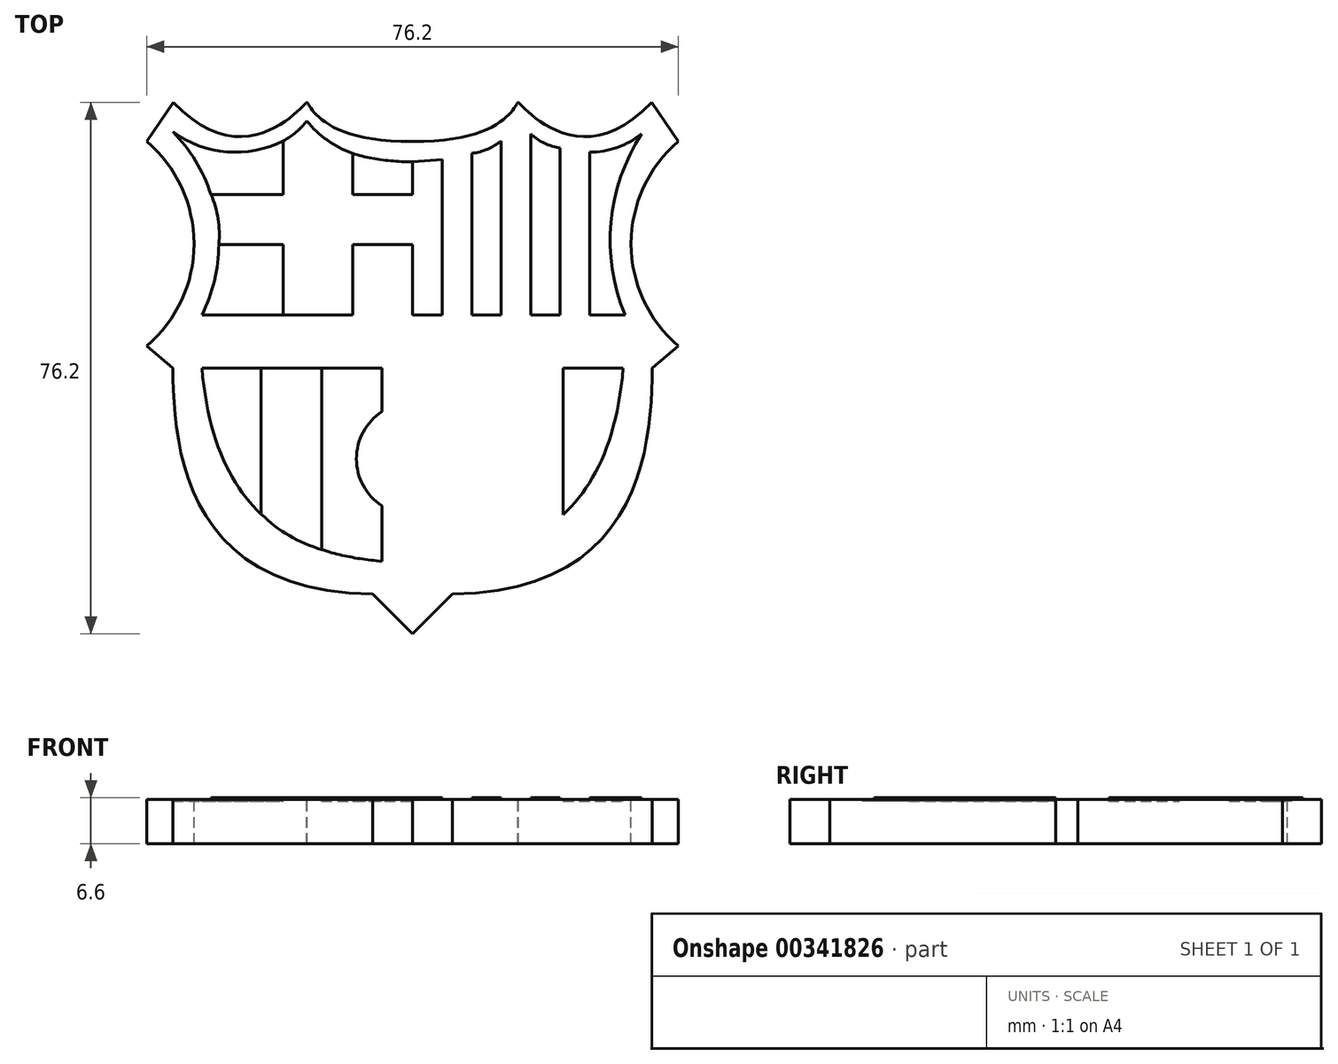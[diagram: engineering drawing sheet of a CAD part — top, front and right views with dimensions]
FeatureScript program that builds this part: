
annotation { "Feature Type Name" : "Feature", "Feature Type Description" : "" }
export const myFeature = defineFeature(function(context is Context, id is Id, definition is map)
    precondition{}
    {
        {
            var Q0;
            Q0=qCreatedBy(makeId("Top.planeOp"),FACE);
            var sketch = newSketch(context, id + "F0", { "sketchPlane" : qUnion([Q0])});
            skLineSegment(sketch, "E0.bottom", {"start": v(-19.05, -38.1) * mm, "end": v(19.05, -38.1) * mm});
            skLineSegment(sketch, "E0.top", {"start": v(-19.05, 38.1) * mm, "end": v(19.05, 38.1) * mm});
            skLineSegment(sketch, "E0.left", {"start": v(-19.05, -38.1) * mm, "end": v(-19.05, 38.1) * mm});
            skLineSegment(sketch, "E0.right", {"start": v(19.05, -38.1) * mm, "end": v(19.05, 38.1) * mm});
            skPoint(sketch, "E0.middle", {"position": v(0, 0) * mm});
            skSolve(sketch);
        }
        {
            var Q0;
            Q0=makeQuery(id+"F0.imprint","IMPRINT",FACE,{"disambiguationData":[TD([[makeQuery(id+"F0.imprint","IMPRINT",EDGE,{"derivedFrom":sQuery(id+"F0.wireOp",EDGE,"E0.bottom")}),1.0]])]});
            extrude(context, id + "F1", {"entities" : qUnion([Q0]), "depth" : 6.35 * mm});
        }
        {
            var Q0;
            Q0=makeQuery(id+"F1.opExtrude","CAP_FACE",FACE,{"disambiguationData":[OSD([sQuery(id+"F0.wireOp",EDGE,"E0.bottom"),sQuery(id+"F0.wireOp",EDGE,"E0.top"),sQuery(id+"F0.wireOp",EDGE,"E0.left"),sQuery(id+"F0.wireOp",EDGE,"E0.right")])],"isStart":false});
            var sketch = newSketch(context, id + "F2", { "sketchPlane" : qUnion([Q0])});
            skArc(sketch, "E1", {"start": v(19.05, 32.51) * mm, "mid": v(12.28, 17.83) * mm, "end": v(19.05, 3.15) * mm});
            skFitSpline(sketch, "E2", {"points": [v(-19.05, 32.51) * mm, v(-3.95, 38.1) * mm, v(-3.79, 38.03) * mm, v(15.22, 38.1) * mm], "startDerivative": vector(85.07, -1.32) * mm, "endDerivative": vector(60.07, 63.46) * mm});
            skLineSegment(sketch, "E3", {"start": v(15.22, 38.1) * mm, "end": v(19.05, 32.51) * mm});
            skLineSegment(sketch, "E4", {"start": v(19.05, 3.15) * mm, "end": v(15.33, 0) * mm});
            skFitSpline(sketch, "E5", {"points": [v(15.33, 0) * mm, v(-13.36, -32.4) * mm], "startDerivative": vector(-0.49, -34.46) * mm, "endDerivative": vector(-81.2, -0.97) * mm});
            skLineSegment(sketch, "E6", {"start": v(-13.36, -32.4) * mm, "end": v(-19.05, -38.1) * mm});
            skLineSegment(sketch, "E7", {"start": v(-19.05, 32.51) * mm, "end": v(-19.05, -38.1) * mm});
            skSolve(sketch);
        }
        {
            var Q0;
            {var subQ0=sQuery(id+"F2.wireOp",EDGE,"E2");var subQ1=makeQuery(id+"F1.opExtrude","CAP_EDGE",EDGE,{"disambiguationData":[OSD([sQuery(id+"F0.wireOp",EDGE,"E0.top")])],"isStart":false});var subQ2=makeQuery(id+"F2.imprint","INTERSECT",VERTEX,{"disambiguationData":[OD(0.0)],"derivedFrom":[subQ1,subQ0]});Q0=makeQuery(id+"F2.imprint","IMPRINT",FACE,{"disambiguationData":[TD([[makeQuery(id+"F2.imprint","IMPRINT",EDGE,{"disambiguationData":[TD([[subQ2,-1.0]])],"derivedFrom":subQ0}),-1.0]])]});}
            var Q1;
            {var subQ1=makeQuery(id+"F1.opExtrude","CAP_EDGE",EDGE,{"disambiguationData":[OSD([sQuery(id+"F0.wireOp",EDGE,"E0.left")])],"isStart":false});var subQ3=makeQuery(id+"F1.opExtrude","CAP_EDGE",EDGE,{"disambiguationData":[OSD([sQuery(id+"F0.wireOp",EDGE,"E0.top")])],"isStart":false});var subQ5=makeQuery(id+"F2.imprint","INTERSECT",VERTEX,{"derivedFrom":[subQ3,subQ1]});Q1=makeQuery(id+"F2.imprint","IMPRINT",FACE,{"disambiguationData":[TD([[makeQuery(id+"F2.imprint","IMPRINT",EDGE,{"disambiguationData":[TD([[subQ5,-1.0]])],"derivedFrom":subQ3}),-1.0]])]});}
            var Q2;
            {var subQ1=sQuery(id+"F2.wireOp",EDGE,"E4");Q2=makeQuery(id+"F2.imprint","IMPRINT",FACE,{"disambiguationData":[TD([[makeQuery(id+"F2.imprint","IMPRINT",EDGE,{"derivedFrom":subQ1}),1.0]])]});}
            var Q3;
            {var subQ0=sQuery(id+"F2.wireOp",EDGE,"E1");Q3=makeQuery(id+"F2.imprint","IMPRINT",FACE,{"disambiguationData":[TD([[makeQuery(id+"F2.imprint","IMPRINT",EDGE,{"derivedFrom":subQ0}),1.0]])]});}
            var Q4;
            {var subQ0=sQuery(id+"F2.wireOp",EDGE,"E3");Q4=makeQuery(id+"F2.imprint","IMPRINT",FACE,{"disambiguationData":[TD([[makeQuery(id+"F2.imprint","IMPRINT",EDGE,{"derivedFrom":subQ0}),1.0]])]});}
            var Q5;
            {var subQ0=sQuery(id+"F2.wireOp",EDGE,"E2");var subQ1=makeQuery(id+"F1.opExtrude","CAP_EDGE",EDGE,{"disambiguationData":[OSD([sQuery(id+"F0.wireOp",EDGE,"E0.top")])],"isStart":false});var subQ3=makeQuery(id+"F2.imprint","INTERSECT",VERTEX,{"disambiguationData":[OD(1.0)],"derivedFrom":[subQ1,subQ0]});Q5=makeQuery(id+"F2.imprint","IMPRINT",FACE,{"disambiguationData":[TD([[makeQuery(id+"F2.imprint","IMPRINT",EDGE,{"disambiguationData":[TD([[subQ3,-1.0]])],"derivedFrom":subQ0}),1.0]])]});}
            extrude(context, id + "F3", {"entities" : qUnion([Q0, Q1, Q2, Q3, Q4, Q5]), "operationType" : NewBodyOperationType.REMOVE, "oppositeDirection" : true, "depth" : 6.35 * mm});
        }
        {
            var Q0;
            Q0=makeQuery(id+"F1.opExtrude","SWEPT_BODY",BODY,{"disambiguationData":[OSD([sQuery(id+"F0.wireOp",EDGE,"E0.bottom"),sQuery(id+"F0.wireOp",EDGE,"E0.top"),sQuery(id+"F0.wireOp",EDGE,"E0.left"),sQuery(id+"F0.wireOp",EDGE,"E0.right")])]});
            var Q1;
            Q1=makeQuery(id+"F1.opExtrude","SWEPT_FACE",FACE,{"disambiguationData":[OSD([sQuery(id+"F0.wireOp",EDGE,"E0.left")])]});
            mirror(context, id + "F4", {"operationType" : NewBodyOperationType.ADD, "entities" : qUnion([Q0]), "mirrorPlane" : qUnion([Q1])});
        }
        {
            var Q0;
            {var subQ0=makeQuery(id+"F1.opExtrude","CAP_FACE",FACE,{"disambiguationData":[OSD([sQuery(id+"F0.wireOp",EDGE,"E0.bottom"),sQuery(id+"F0.wireOp",EDGE,"E0.top"),sQuery(id+"F0.wireOp",EDGE,"E0.left"),sQuery(id+"F0.wireOp",EDGE,"E0.right")])],"isStart":false});Q0=makeQuery(id+"F4.boolean.opBoolean","MERGE",FACE,{"derivedFrom":[subQ0,makeQuery(id+"F4.opPattern","COPY",FACE,{"derivedFrom":subQ0,"instanceName":"1"})]});}
            var sketch = newSketch(context, id + "F5", { "sketchPlane" : qUnion([Q0])});
            skArc(sketch, "E8", {"start": v(-53.4, 33.87) * mm, "mid": v(-43.7, 30.98) * mm, "end": v(-34.33, 34.8) * mm});
            skArc(sketch, "E9", {"start": v(15.17, 33.73) * mm, "mid": v(5.65, 30.98) * mm, "end": v(-3.56, 34.66) * mm});
            skFitSpline(sketch, "E10", {"points": [v(-34.33, 34.8) * mm, v(-3.56, 34.66) * mm], "startDerivative": vector(16.22, -20.16) * mm, "endDerivative": vector(21, 21.01) * mm});
            skArc(sketch, "E11", {"start": v(15.17, 33.73) * mm, "mid": v(9, 21.31) * mm, "end": v(11.14, 7.6) * mm});
            skArc(sketch, "E12", {"start": v(-53.4, 33.87) * mm, "mid": v(-47.11, 21.4) * mm, "end": v(-49.24, 7.6) * mm});
            skLineSegment(sketch, "E13", {"start": v(-49.24, 7.6) * mm, "end": v(11.14, 7.6) * mm});
            skLineSegment(sketch, "E14", {"start": v(-49.24, 0) * mm, "end": v(11.14, 0) * mm});
            skFitSpline(sketch, "E15", {"points": [v(-49.24, 0) * mm, v(-19.05, -27.87) * mm, v(11.14, 0) * mm], "startDerivative": vector(11.4, -138.75) * mm, "endDerivative": vector(11.4, 138.75) * mm});
            skLineSegment(sketch, "E16", {"start": v(-49.24, 0) * mm, "end": v(-40.74, 0) * mm});
            skLineSegment(sketch, "E17", {"start": v(-40.74, 0) * mm, "end": v(-40.74, -20.94) * mm});
            skLineSegment(sketch, "E18", {"start": v(-40.74, 0) * mm, "end": v(-32.09, 0) * mm});
            skLineSegment(sketch, "E19", {"start": v(-32.09, 0) * mm, "end": v(-32.09, -26.01) * mm});
            skLineSegment(sketch, "E20", {"start": v(-32.09, 0) * mm, "end": v(-23.43, 0) * mm});
            skLineSegment(sketch, "E21", {"start": v(-23.43, 0) * mm, "end": v(-14.78, 0) * mm});
            skLineSegment(sketch, "E22", {"start": v(-14.78, 0) * mm, "end": v(-6.12, 0) * mm});
            skLineSegment(sketch, "E23", {"start": v(-6.12, 0) * mm, "end": v(-6.12, -26.05) * mm});
            skLineSegment(sketch, "E24", {"start": v(-6.12, 0) * mm, "end": v(2.53, 0) * mm});
            skLineSegment(sketch, "E25", {"start": v(2.53, 0) * mm, "end": v(2.53, -21.04) * mm});
            skCircle(sketch, "E26", {"center": v(-19.05, -13) * mm, "radius": 8.05 * mm});
            skPoint(sketch, "E26.centerSnap0", {"position": v(-32.09, -13) * mm});
            skLineSegment(sketch, "E27", {"start": v(-23.43, 0) * mm, "end": v(-23.43, -6.26) * mm});
            skLineSegment(sketch, "E28", {"start": v(-23.43, -19.75) * mm, "end": v(-23.43, -27.7) * mm});
            skLineSegment(sketch, "E29", {"start": v(-14.78, 0) * mm, "end": v(-14.78, -6.19) * mm});
            skLineSegment(sketch, "E30", {"start": v(-14.78, -19.82) * mm, "end": v(-14.78, -27.7) * mm});
            skLineSegment(sketch, "E31", {"start": v(-19.05, 7.6) * mm, "end": v(-19.05, 29.58) * mm});
            skLineSegment(sketch, "E32", {"start": v(-19.05, 7.6) * mm, "end": v(-14.78, 7.6) * mm});
            skLineSegment(sketch, "E33", {"start": v(-14.78, 7.6) * mm, "end": v(-10.56, 7.6) * mm});
            skLineSegment(sketch, "E34", {"start": v(-10.56, 7.6) * mm, "end": v(-6.33, 7.6) * mm});
            skLineSegment(sketch, "E35", {"start": v(-6.33, 7.6) * mm, "end": v(-2.11, 7.6) * mm});
            skLineSegment(sketch, "E36", {"start": v(-2.11, 7.6) * mm, "end": v(2.11, 7.6) * mm});
            skLineSegment(sketch, "E37", {"start": v(2.11, 7.6) * mm, "end": v(6.33, 7.6) * mm});
            skLineSegment(sketch, "E38", {"start": v(6.33, 7.6) * mm, "end": v(6.33, 30.96) * mm});
            skLineSegment(sketch, "E39", {"start": v(2.11, 7.6) * mm, "end": v(2.11, 31.57) * mm});
            skLineSegment(sketch, "E40", {"start": v(-2.11, 7.6) * mm, "end": v(-2.11, 33.56) * mm});
            skLineSegment(sketch, "E41", {"start": v(-6.33, 7.6) * mm, "end": v(-6.33, 32.57) * mm});
            skLineSegment(sketch, "E42", {"start": v(-10.56, 6.12) * mm, "end": v(-10.56, 30.78) * mm});
            skLineSegment(sketch, "E43", {"start": v(-14.78, 7.6) * mm, "end": v(-14.78, 29.88) * mm});
            skLineSegment(sketch, "E44.bottom", {"start": v(-19.05, 7.6) * mm, "end": v(-27.66, 7.6) * mm});
            skLineSegment(sketch, "E44.top", {"start": v(-19.05, 17.73) * mm, "end": v(-27.66, 17.73) * mm});
            skLineSegment(sketch, "E44.left", {"start": v(-19.05, 7.6) * mm, "end": v(-19.05, 17.73) * mm});
            skLineSegment(sketch, "E44.right", {"start": v(-27.66, 7.6) * mm, "end": v(-27.66, 17.73) * mm});
            skLineSegment(sketch, "E45", {"start": v(-27.66, 30.77) * mm, "end": v(-27.66, 24.91) * mm});
            skLineSegment(sketch, "E46", {"start": v(-27.66, 24.91) * mm, "end": v(-19.05, 24.91) * mm});
            skLineSegment(sketch, "E47", {"start": v(-27.66, 7.6) * mm, "end": v(-37.58, 7.6) * mm});
            skLineSegment(sketch, "E48", {"start": v(-37.58, 7.6) * mm, "end": v(-37.58, 17.73) * mm});
            skLineSegment(sketch, "E49", {"start": v(-37.58, 17.73) * mm, "end": v(-46.83, 17.73) * mm});
            skLineSegment(sketch, "E50", {"start": v(-37.58, 24.91) * mm, "end": v(-37.58, 32.6) * mm});
            skLineSegment(sketch, "E51", {"start": v(-37.58, 24.91) * mm, "end": v(-47.95, 24.91) * mm});
            skSolve(sketch);
        }
        {
            var Q0;
            {var subQ3=sQuery(id+"F5.wireOp",EDGE,"E50");Q0=makeQuery(id+"F5.imprint","IMPRINT",FACE,{"disambiguationData":[TD([[makeQuery(id+"F5.imprint","IMPRINT",EDGE,{"derivedFrom":subQ3}),1.0]])]});}
            var Q1;
            {var subQ4=sQuery(id+"F5.wireOp",EDGE,"E48");Q1=makeQuery(id+"F5.imprint","IMPRINT",FACE,{"disambiguationData":[TD([[makeQuery(id+"F5.imprint","IMPRINT",EDGE,{"derivedFrom":subQ4}),1.0]])]});}
            var Q2;
            Q2=makeQuery(id+"F5.imprint","IMPRINT",FACE,{"disambiguationData":[TD([[makeQuery(id+"F5.imprint","IMPRINT",EDGE,{"derivedFrom":sQuery(id+"F5.wireOp",EDGE,"E44.bottom")}),-1.0]])]});
            var Q3;
            {var subQ3=sQuery(id+"F5.wireOp",EDGE,"E45");Q3=makeQuery(id+"F5.imprint","IMPRINT",FACE,{"disambiguationData":[TD([[makeQuery(id+"F5.imprint","IMPRINT",EDGE,{"derivedFrom":subQ3}),1.0]])]});}
            var Q4;
            {var subQ4=sQuery(id+"F5.wireOp",EDGE,"E33");Q4=makeQuery(id+"F5.imprint","IMPRINT",FACE,{"disambiguationData":[TD([[makeQuery(id+"F5.imprint","IMPRINT",EDGE,{"derivedFrom":subQ4}),1.0]])]});}
            var Q5;
            Q5=makeQuery(id+"F5.imprint","IMPRINT",FACE,{"disambiguationData":[TD([[makeQuery(id+"F5.imprint","IMPRINT",EDGE,{"derivedFrom":sQuery(id+"F5.wireOp",EDGE,"E35")}),1.0]])]});
            var Q6;
            Q6=makeQuery(id+"F5.imprint","IMPRINT",FACE,{"disambiguationData":[TD([[makeQuery(id+"F5.imprint","IMPRINT",EDGE,{"derivedFrom":sQuery(id+"F5.wireOp",EDGE,"E37")}),1.0]])]});
            var Q7;
            {var subQ0=sQuery(id+"F5.wireOp",EDGE,"E14");Q7=makeQuery(id+"F5.imprint","IMPRINT",FACE,{"disambiguationData":[TD([[makeQuery(id+"F5.imprint","IMPRINT",EDGE,{"derivedFrom":subQ0}),-1.0]])]});}
            var Q8;
            Q8=makeQuery(id+"F5.imprint","IMPRINT",FACE,{"disambiguationData":[TD([[makeQuery(id+"F5.imprint","IMPRINT",EDGE,{"derivedFrom":sQuery(id+"F5.wireOp",EDGE,"E22")}),-1.0]])]});
            var Q9;
            {var subQ3=sQuery(id+"F5.wireOp",EDGE,"E19");Q9=makeQuery(id+"F5.imprint","IMPRINT",FACE,{"disambiguationData":[TD([[makeQuery(id+"F5.imprint","IMPRINT",EDGE,{"derivedFrom":subQ3}),1.0]])]});}
            var Q10;
            {var subQ0=sQuery(id+"F5.wireOp",EDGE,"E16");Q10=makeQuery(id+"F5.imprint","IMPRINT",FACE,{"disambiguationData":[TD([[makeQuery(id+"F5.imprint","IMPRINT",EDGE,{"derivedFrom":subQ0}),-1.0]])]});}
            extrude(context, id + "F6", {"entities" : qUnion([Q0, Q1, Q2, Q3, Q4, Q5, Q6, Q7, Q8, Q9, Q10]), "operationType" : NewBodyOperationType.REMOVE, "oppositeDirection" : true, "depth" : 0.25 * mm});
        }
        {
            var Q0;
            {var subQ0=makeQuery(id+"F1.opExtrude","CAP_FACE",FACE,{"disambiguationData":[OSD([sQuery(id+"F0.wireOp",EDGE,"E0.bottom"),sQuery(id+"F0.wireOp",EDGE,"E0.top"),sQuery(id+"F0.wireOp",EDGE,"E0.left"),sQuery(id+"F0.wireOp",EDGE,"E0.right")])],"isStart":false});Q0=makeQuery(id+"F4.boolean.opBoolean","MERGE",FACE,{"derivedFrom":[subQ0,makeQuery(id+"F4.opPattern","COPY",FACE,{"derivedFrom":subQ0,"instanceName":"1"})]});}
            var sketch = newSketch(context, id + "F7", { "sketchPlane" : qUnion([Q0])});
            skLineSegment(sketch, "E52", {"start": v(-37.58, 7.6) * mm, "end": v(-27.66, 7.6) * mm});
            skLineSegment(sketch, "E53", {"start": v(-27.66, 7.6) * mm, "end": v(-27.66, 17.73) * mm});
            skLineSegment(sketch, "E54", {"start": v(-27.66, 17.73) * mm, "end": v(-19.05, 17.73) * mm});
            skLineSegment(sketch, "E55", {"start": v(-19.05, 17.73) * mm, "end": v(-19.05, 24.91) * mm});
            skLineSegment(sketch, "E56", {"start": v(-19.05, 24.91) * mm, "end": v(-27.66, 24.91) * mm});
            skLineSegment(sketch, "E57", {"start": v(-27.66, 24.91) * mm, "end": v(-27.66, 30.77) * mm});
            skArc(sketch, "E58", {"start": v(-46.83, 17.73) * mm, "mid": v(-46.93, 21.4) * mm, "end": v(-47.95, 24.91) * mm});
            skArc(sketch, "E59", {"start": v(-40.74, -20.94) * mm, "mid": v(-36.74, -24.02) * mm, "end": v(-32.09, -26.01) * mm});
            skArc(sketch, "E60", {"start": v(-23.43, -27.7) * mm, "mid": v(-19.1, -28.08) * mm, "end": v(-14.78, -27.7) * mm});
            skArc(sketch, "E61", {"start": v(-6.12, -26.05) * mm, "mid": v(-1.39, -24.25) * mm, "end": v(2.53, -21.04) * mm});
            skLineSegment(sketch, "E62", {"start": v(-47.95, 24.91) * mm, "end": v(-37.58, 24.91) * mm});
            skLineSegment(sketch, "E63", {"start": v(-37.58, 24.91) * mm, "end": v(-37.58, 32.6) * mm});
            skLineSegment(sketch, "E64", {"start": v(-46.83, 17.73) * mm, "end": v(-37.58, 17.73) * mm});
            skLineSegment(sketch, "E65", {"start": v(-37.58, 17.73) * mm, "end": v(-37.58, 7.6) * mm});
            skLineSegment(sketch, "E66", {"start": v(-40.74, 0) * mm, "end": v(-32.09, 0) * mm});
            skLineSegment(sketch, "E67", {"start": v(-32.09, 0) * mm, "end": v(-32.09, -26.01) * mm});
            skLineSegment(sketch, "E68", {"start": v(-40.74, 0) * mm, "end": v(-40.74, -20.94) * mm});
            skLineSegment(sketch, "E69", {"start": v(-23.43, 0) * mm, "end": v(-14.78, 0) * mm});
            skLineSegment(sketch, "E70", {"start": v(-6.12, 0) * mm, "end": v(2.53, 0) * mm});
            skLineSegment(sketch, "E71", {"start": v(-19.05, 7.6) * mm, "end": v(-14.78, 7.6) * mm});
            skLineSegment(sketch, "E72", {"start": v(-14.78, 7.6) * mm, "end": v(-14.78, 29.88) * mm});
            skLineSegment(sketch, "E73", {"start": v(-14.78, 29.88) * mm, "end": v(-19.05, 29.58) * mm});
            skLineSegment(sketch, "E74", {"start": v(-19.05, 29.58) * mm, "end": v(-19.05, 7.6) * mm});
            skLineSegment(sketch, "E75", {"start": v(-10.56, 7.6) * mm, "end": v(-6.33, 7.6) * mm});
            skLineSegment(sketch, "E76", {"start": v(-6.33, 7.6) * mm, "end": v(-6.33, 32.57) * mm});
            skArc(sketch, "E77", {"start": v(-10.56, 30.78) * mm, "mid": v(-8.32, 31.38) * mm, "end": v(-6.33, 32.57) * mm});
            skLineSegment(sketch, "E78", {"start": v(-10.56, 30.78) * mm, "end": v(-10.56, 7.6) * mm});
            skLineSegment(sketch, "E79", {"start": v(-2.11, 7.6) * mm, "end": v(2.11, 7.6) * mm});
            skLineSegment(sketch, "E80", {"start": v(2.11, 7.6) * mm, "end": v(2.11, 31.57) * mm});
            skLineSegment(sketch, "E81", {"start": v(-2.11, 7.6) * mm, "end": v(-2.11, 33.56) * mm});
            skArc(sketch, "E82", {"start": v(-2.11, 33.56) * mm, "mid": v(-0.15, 32.25) * mm, "end": v(2.11, 31.57) * mm});
            skArc(sketch, "E83", {"start": v(6.33, 30.96) * mm, "mid": v(10.29, 31.63) * mm, "end": v(13.79, 33.59) * mm});
            skLineSegment(sketch, "E84", {"start": v(6.33, 7.6) * mm, "end": v(11.4, 7.6) * mm});
            skArc(sketch, "E85", {"start": v(13.79, 33.59) * mm, "mid": v(9.4, 20.9) * mm, "end": v(11.4, 7.6) * mm});
            skLineSegment(sketch, "E86", {"start": v(6.33, 30.96) * mm, "end": v(6.33, 7.6) * mm});
            skPoint(sketch, "E87", {"position": v(-34.2, 35.45) * mm});
            skArc(sketch, "E88", {"start": v(-37.58, 32.6) * mm, "mid": v(-35.73, 33.83) * mm, "end": v(-34.2, 35.45) * mm});
            skArc(sketch, "E89", {"start": v(-34.2, 35.45) * mm, "mid": v(-31.25, 32.66) * mm, "end": v(-27.66, 30.77) * mm});
            skSolve(sketch);
        }
        {
            var Q0;
            Q0=makeQuery(id+"F7.imprint","IMPRINT",FACE,{"disambiguationData":[TD([[makeQuery(id+"F7.imprint","IMPRINT",EDGE,{"derivedFrom":sQuery(id+"F7.wireOp",EDGE,"E59")}),1.0]])]});
            var Q1;
            Q1=makeQuery(id+"F7.imprint","IMPRINT",FACE,{"disambiguationData":[TD([[makeQuery(id+"F7.imprint","IMPRINT",EDGE,{"derivedFrom":sQuery(id+"F7.wireOp",EDGE,"E75")}),1.0]])]});
            var Q2;
            Q2=makeQuery(id+"F7.imprint","IMPRINT",FACE,{"disambiguationData":[TD([[makeQuery(id+"F7.imprint","IMPRINT",EDGE,{"derivedFrom":sQuery(id+"F7.wireOp",EDGE,"E79")}),1.0]])]});
            var Q3;
            {var subQ4=sQuery(id+"F7.wireOp",EDGE,"E71");Q3=makeQuery(id+"F7.imprint","IMPRINT",FACE,{"disambiguationData":[TD([[makeQuery(id+"F7.imprint","IMPRINT",EDGE,{"derivedFrom":subQ4}),1.0]])]});}
            var Q4;
            Q4=makeQuery(id+"F7.imprint","IMPRINT",FACE,{"disambiguationData":[TD([[makeQuery(id+"F7.imprint","IMPRINT",EDGE,{"derivedFrom":sQuery(id+"F7.wireOp",EDGE,"E61")}),1.0]])]});
            var Q5;
            Q5=makeQuery(id+"F7.imprint","IMPRINT",FACE,{"disambiguationData":[TD([[makeQuery(id+"F7.imprint","IMPRINT",EDGE,{"derivedFrom":sQuery(id+"F7.wireOp",EDGE,"E60")}),1.0]])]});
            var Q6;
            Q6=makeQuery(id+"F7.imprint","IMPRINT",FACE,{"disambiguationData":[TD([[makeQuery(id+"F7.imprint","IMPRINT",EDGE,{"derivedFrom":sQuery(id+"F7.wireOp",EDGE,"E83")}),-1.0]])]});
            var Q7;
            Q7=makeQuery(id+"F7.imprint","IMPRINT",FACE,{"disambiguationData":[TD([[makeQuery(id+"F7.imprint","IMPRINT",EDGE,{"derivedFrom":sQuery(id+"F7.wireOp",EDGE,"E52")}),1.0]])]});
            extrude(context, id + "F8", {"entities" : qUnion([Q0, Q1, Q2, Q3, Q4, Q5, Q6, Q7]), "operationType" : NewBodyOperationType.ADD, "depth" : 0.25 * mm});
        }
    });
